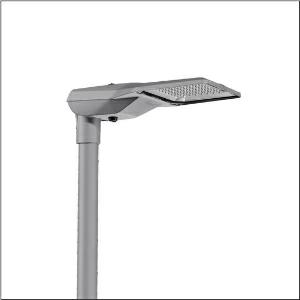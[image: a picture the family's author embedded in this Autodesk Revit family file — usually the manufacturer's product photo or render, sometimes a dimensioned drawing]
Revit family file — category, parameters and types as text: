
# Revit family: streetlight_sl_21_iq_midi___p1_0a_5xe3a31y08mb_7489
name_source: partatom
category: Lighting Fixtures
units: mm (PartAtom-declared; Revit-internal decimal feet)

## family parameters
Cut with Voids When Loaded = No
Host = Face
Light Source = No
Part Type = Normal
Room Calculation Point = No
Round Connector Dimension = Use Diameter
Shared = No

## types (1)
- --- (1 x LED, 18340 lm, 129.3 W, 3000K)
    Apparent Load = 129 VA
    CIE Flux Codes = 21 50 90 100 100
    Color Rendering = 70
    Color Temperature = 3000K
    Default Elevation = 1800 mm
    Description = Streetlight SL 21 iQ midi, mast luminaire, primary light control with lens, of PMMA, primary optical cover: cover, of toughened safety glass, transparent, light distribution: P1.0a, light emission: direct distribution, primary light characteristic: asymmetric, installation type: post-top, side-entry, LED, High Power LED, rated luminous flux: 18.340lm, luminous efficacy: 142lm/W, light colour: 730, colour temperature: 3000K, control: presetting dimming logarithmic, Street-Remote, Auto-Match, Temp-Guard, Lumen-Switch, Night-Set, Smart-Wire, Light-Fading, Desk-Remote (wireless, voltage-free reading and setting of iQ features in the workshop via application-optimized NFC function/RFID function), optimised constant luminous flux control (CLO 2.0), mains connection: 230..240V, AC, 50/60Hz, start of lifetime: 129W, end of service life: 142W, reduction: 56W, luminaire housing, of diecast aluminium, powder-coated, Siteco® metallic grey (DB 702S), corrosivity category C5 mid according to DIN EN ISO 12944, please order mast flange separately, inclination adjustable: 0°, 5°, 10°, 15°, sealing non-destructively replaceable, multi-level sealing system, length: 644mm, width: 335mm, height: 110mm, mast flange for spigot size: 42mm (side-entry): 5XC10008XM4, 60/48mm (side-entry/post-top): 5XC10108XM2, 76/60mm (side-entry/post-top): 5XC10108XM1, Smart Interface below and above, protection rating (complete): IP66, insulation class (complete): insulation class II (safety insulation), certification: CE, ENEC, ENEC+, VDE, impact resistance: IK09, permissible operating ambient temperature for outdoor applications: -40..+50°C, standard-compliant lighting for roads and squares, packaging unit: 1 piece

Light Distribution: P1.0a
    Height = 111 mm
    Lamp = 1 x LED
    Lamp Light Flux = 18340 lm
    Lamp Power = 129.3 W
    Lamp count = 1
    Length = 644 mm
    Luminous efficacy = 142 lm/W
    Manufacturer = Siteco
    ModVariant = No
    Model = 5XE3A31Y08MB
    Number of Poles = 1
    OnlyDefault = Yes
    Power Factor = 1
    Product Name = Streetlight SL 21 iQ midi | P1.0a
    Product group = mast luminaire | pylon top
    ProductGroupID = 6100
    Protection Class = Protection class II
    Protection Degree = IP 66
    RLX_Detail_Level = 1
    RLX_Emergency_Light_Flux = 0 lm
    RLX_Emergency_Type = 0
    RLX_Emergency_Type_DB = No
    RlxData = <blob elided: 102065 chars, md5=15a29f46>
    Socket = socket
    Standby Power = 0 W
    System Light Flux = 18340 lm
    System Power = 129 W
    Type Comments = factory setting: luminous flux: 100 % | dim-lin: 254 | 672 mA
    Type Image = l_1004304.jpg
    URL = http://relux.com
    VarID = @adj_043501
    Voltage = 0 V
    Weight = 0.00 kg
    Width = 336 mm

## geometry (parser evidence)
native form markers: Blend x4, Sweep x10
no freeform markers — native parametric forms only
